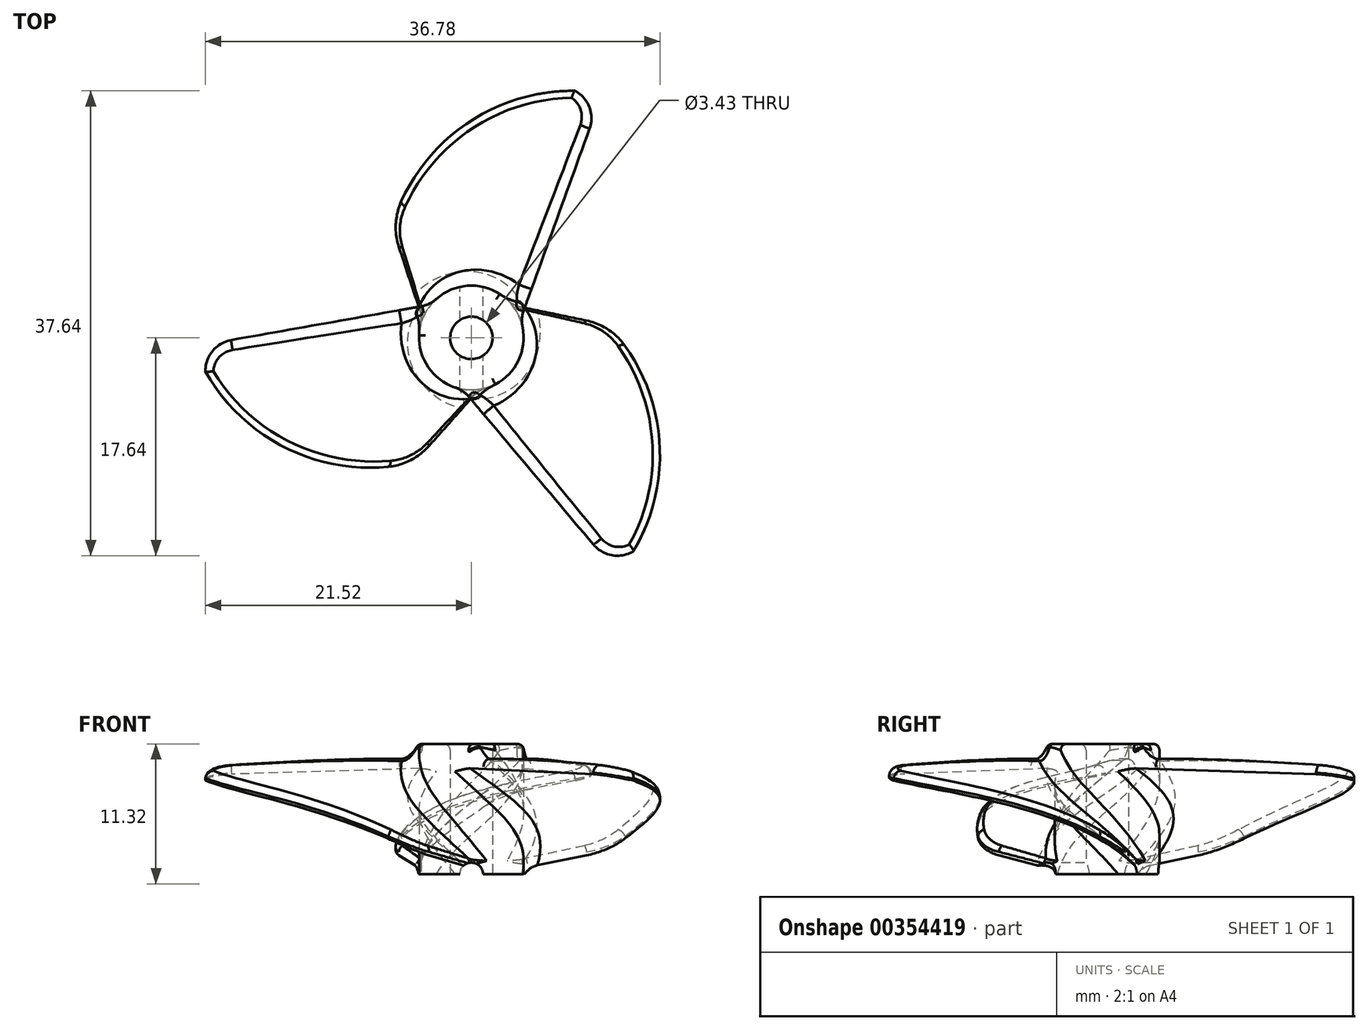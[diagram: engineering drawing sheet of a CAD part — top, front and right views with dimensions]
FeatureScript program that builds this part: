
annotation { "Feature Type Name" : "Feature", "Feature Type Description" : "" }
export const myFeature = defineFeature(function(context is Context, id is Id, definition is map)
    precondition{}
    {
        {
            var Q0;
            Q0=qCreatedBy(makeId("Top.planeOp"),FACE);
            var sketch = newSketch(context, id + "F0", { "sketchPlane" : qUnion([Q0])});
            skCircle(sketch, "E0", {"center": v(0, 0) * mm, "radius": 4.23 * mm});
            skSolve(sketch);
        }
        {
            var Q0;
            Q0 = qSketchRegion(id + "F0", true);
            extrude(context, id + "F1", {"entities" : qUnion([Q0]), "depth" : 10.54 * mm});
        }
        {
            var Q0;
            Q0=qCreatedBy(makeId("Front.planeOp"),FACE);
            var sketch = newSketch(context, id + "F2", { "sketchPlane" : qUnion([Q0])});
            skLineSegment(sketch, "E1", {"start": v(3.43, 10.54) * mm, "end": v(-3.43, 0.5) * mm});
            skLineSegment(sketch, "E2", {"start": v(-3.43, 0) * mm, "end": v(3.43, 8.64) * mm});
            skLineSegment(sketch, "E3", {"start": v(3.43, 8.64) * mm, "end": v(3.43, 10.54) * mm});
            skLineSegment(sketch, "E4", {"start": v(3.43, 10.54) * mm, "end": v(0, 10.54) * mm, "construction": true});
            skLineSegment(sketch, "E5", {"start": v(0, 10.54) * mm, "end": v(-3.43, 10.54) * mm, "construction": true});
            skLineSegment(sketch, "E6", {"start": v(-3.43, 10.54) * mm, "end": v(-3.43, 0.5) * mm, "construction": true});
            skLineSegment(sketch, "E7", {"start": v(-3.43, 0) * mm, "end": v(-3.43, 0.5) * mm});
            skSolve(sketch);
        }
        {
            var Q0;
            Q0=qCreatedBy(makeId("Front.planeOp"),FACE);
            cPlane(context, id + "F3", {"entities" : qUnion([Q0]), "cplaneType" : CPlaneType.OFFSET, "offset" : 20.32 * mm, "oppositeDirection" : true, "width" : 152.4 * mm, "height" : 152.4 * mm});
        }
        {
            var Q0;
            Q0=qCreatedBy(id+"F3.planeOp",FACE);
            var sketch = newSketch(context, id + "F4", { "sketchPlane" : qUnion([Q0])});
            skLineSegment(sketch, "E8", {"start": v(10.8, 8.76) * mm, "end": v(-10.16, 5) * mm});
            skLineSegment(sketch, "E9", {"start": v(-10.16, 5) * mm, "end": v(-10.16, 4.22) * mm});
            skLineSegment(sketch, "E10", {"start": v(-10.16, 4.22) * mm, "end": v(10.8, 7.99) * mm});
            skLineSegment(sketch, "E11", {"start": v(10.8, 7.99) * mm, "end": v(10.8, 8.76) * mm});
            skSolve(sketch);
        }
        {
            var Q0;
            Q0=makeQuery(id+"F2.imprint","IMPRINT",FACE,{"disambiguationData":[TD([[makeQuery(id+"F2.imprint","IMPRINT",EDGE,{"derivedFrom":sQuery(id+"F2.wireOp",EDGE,"E1")}),1.0]])]});
            var Q1;
            Q1=makeQuery(id+"F4.imprint","IMPRINT",FACE,{"disambiguationData":[TD([[makeQuery(id+"F4.imprint","IMPRINT",EDGE,{"derivedFrom":sQuery(id+"F4.wireOp",EDGE,"E8")}),1.0]])]});
            loft(context, id + "F5", {"sheetProfilesArray" : [{ "sheetProfileEntities" : qUnion([Q0]) }, { "sheetProfileEntities" : qUnion([Q1]) }]});
        }
        {
            var Q0;
            Q0=makeQuery(id+"F5.opLoft","MID_CAP_EDGE",EDGE,{"disambiguationData":[OSD([sQuery(id+"F4.wireOp",EDGE,"E8"),sQuery(id+"F4.wireOp",EDGE,"E10"),sQuery(id+"F4.wireOp",EDGE,"E11")])],"capPos":1.0});
            fillet(context, id + "F6", {"entities" : qUnion([Q0]), "radius" : 2.54 * mm, "tangentPropagation" : true, "allowEdgeOverflow" : false});
        }
        {
            var Q0;
            Q0=qCreatedBy(makeId("Top.planeOp"),FACE);
            var sketch = newSketch(context, id + "F7", { "sketchPlane" : qUnion([Q0])});
            skArc(sketch, "E12", {"start": v(10.23, 19.86) * mm, "mid": v(-0.6, 17.2) * mm, "end": v(-6.71, 7.88) * mm});
            skLineSegment(sketch, "E13", {"start": v(-6.71, 7.88) * mm, "end": v(-17.65, 28.01) * mm});
            skLineSegment(sketch, "E14", {"start": v(-17.65, 28.01) * mm, "end": v(12.3, 32.12) * mm});
            skLineSegment(sketch, "E15", {"start": v(12.3, 32.12) * mm, "end": v(10.23, 19.86) * mm});
            skSolve(sketch);
        }
        {
            var Q0;
            Q0 = qSketchRegion(id + "F7", true);
            extrude(context, id + "F8", {"entities" : qUnion([Q0]), "operationType" : NewBodyOperationType.REMOVE, "depth" : 50.8 * mm});
        }
        {
            var Q0;
            Q0=makeQuery(id+"F8.boolean.opBoolean","INTERSECT",EDGE,{"derivedFrom":[makeQuery(id+"F5.opLoft","SWEPT_FACE",FACE,{"disambiguationData":[OSD([sQuery(id+"F2.wireOp",EDGE,"E1"),sQuery(id+"F2.wireOp",EDGE,"vgnnuIFg-lXOL-v0tE-bj0G-pIZIy2lSMrQo"),sQuery(id+"F2.wireOp",EDGE,"E2"),sQuery(id+"F4.wireOp",EDGE,"E8"),sQuery(id+"F4.wireOp",EDGE,"E9"),sQuery(id+"F4.wireOp",EDGE,"E10")])]}),makeQuery(id+"F8.opExtrude","SWEPT_FACE",FACE,{"disambiguationData":[OSD([sQuery(id+"F7.wireOp",EDGE,"E12")])]})]});
            fillet(context, id + "F9", {"entities" : qUnion([Q0]), "radius" : 5.08 * mm, "tangentPropagation" : true, "allowEdgeOverflow" : false});
        }
        {
            var Q0;
            Q0=makeQuery(id+"F1.opExtrude","SWEPT_BODY",BODY,{"disambiguationData":[OSD([sQuery(id+"F0.wireOp",EDGE,"E0")])]});
            var Q1;
            Q1=makeQuery(id+"F5.opLoft","SWEPT_BODY",BODY,{"disambiguationData":[OSD([makeQuery(id+"F2.imprint","IMPRINT",FACE,{"disambiguationData":[TD([[makeQuery(id+"F2.imprint","IMPRINT",EDGE,{"derivedFrom":sQuery(id+"F2.wireOp",EDGE,"E1")}),1.0]])]}),makeQuery(id+"F4.imprint","IMPRINT",FACE,{"disambiguationData":[TD([[makeQuery(id+"F4.imprint","IMPRINT",EDGE,{"derivedFrom":sQuery(id+"F4.wireOp",EDGE,"E8")}),1.0]])]})])]});
            booleanBodies(context, id + "F10", {"operationType" : BooleanOperationType.UNION, "tools" : qUnion([Q0, Q1])});
        }
        {
            var Q0;
            Q0=makeQuery(id+"F10.opBoolean","INTERSECT",EDGE,{"derivedFrom":[makeQuery(id+"F1.opExtrude","SWEPT_FACE",FACE,{"disambiguationData":[OSD([sQuery(id+"F0.wireOp",EDGE,"E0")])]}),makeQuery(id+"F5.opLoft","SWEPT_FACE",FACE,{"disambiguationData":[OSD([sQuery(id+"F2.wireOp",EDGE,"vgnnuIFg-lXOL-v0tE-bj0G-pIZIy2lSMrQo"),sQuery(id+"F2.wireOp",EDGE,"E2"),sQuery(id+"F2.wireOp",EDGE,"E3"),sQuery(id+"F4.wireOp",EDGE,"E9"),sQuery(id+"F4.wireOp",EDGE,"E10"),sQuery(id+"F4.wireOp",EDGE,"E11")])]})]});
            var Q1;
            Q1=makeQuery(id+"F10.opBoolean","INTERSECT",EDGE,{"derivedFrom":[makeQuery(id+"F1.opExtrude","SWEPT_FACE",FACE,{"disambiguationData":[OSD([sQuery(id+"F0.wireOp",EDGE,"E0")])]}),makeQuery(id+"F5.opLoft","SWEPT_FACE",FACE,{"disambiguationData":[OSD([sQuery(id+"F2.wireOp",EDGE,"E1"),sQuery(id+"F2.wireOp",EDGE,"vgnnuIFg-lXOL-v0tE-bj0G-pIZIy2lSMrQo"),sQuery(id+"F2.wireOp",EDGE,"E3"),sQuery(id+"F4.wireOp",EDGE,"E8"),sQuery(id+"F4.wireOp",EDGE,"E9"),sQuery(id+"F4.wireOp",EDGE,"E11")])]})]});
            fillet(context, id + "F11", {"entities" : qUnion([Q0, Q1]), "radius" : 1.27 * mm, "tangentPropagation" : true, "allowEdgeOverflow" : false});
        }
        {
            var Q0;
            Q0=makeQuery(id+"F10.opBoolean","INTERSECT",EDGE,{"derivedFrom":[makeQuery(id+"F1.opExtrude","SWEPT_FACE",FACE,{"disambiguationData":[OSD([sQuery(id+"F0.wireOp",EDGE,"E0")])]}),makeQuery(id+"F5.opLoft","SWEPT_FACE",FACE,{"disambiguationData":[OSD([sQuery(id+"F2.wireOp",EDGE,"E1"),sQuery(id+"F2.wireOp",EDGE,"E2"),sQuery(id+"F2.wireOp",EDGE,"E3"),sQuery(id+"F4.wireOp",EDGE,"E8"),sQuery(id+"F4.wireOp",EDGE,"E10"),sQuery(id+"F4.wireOp",EDGE,"E11")])]})]});
            fillet(context, id + "F12", {"entities" : qUnion([Q0]), "radius" : 2.54 * mm, "tangentPropagation" : true, "allowEdgeOverflow" : false});
        }
        {
            var Q0;
            Q0=makeQuery(id+"F10.opBoolean","INTERSECT",EDGE,{"derivedFrom":[makeQuery(id+"F1.opExtrude","SWEPT_FACE",FACE,{"disambiguationData":[OSD([sQuery(id+"F0.wireOp",EDGE,"E0")])]}),makeQuery(id+"F5.opLoft","SWEPT_FACE",FACE,{"disambiguationData":[OSD([sQuery(id+"F2.wireOp",EDGE,"E1"),sQuery(id+"F2.wireOp",EDGE,"vgnnuIFg-lXOL-v0tE-bj0G-pIZIy2lSMrQo"),sQuery(id+"F2.wireOp",EDGE,"E2"),sQuery(id+"F4.wireOp",EDGE,"E8"),sQuery(id+"F4.wireOp",EDGE,"E9"),sQuery(id+"F4.wireOp",EDGE,"E10")])]})]});
            fillet(context, id + "F13", {"entities" : qUnion([Q0]), "radius" : 2.54 * mm, "tangentPropagation" : true, "allowEdgeOverflow" : false});
        }
        {
            var Q0;
            Q0=makeQuery(id+"F5.opLoft","SWEPT_EDGE",EDGE,{"disambiguationData":[OSD([sQuery(id+"F2.wireOp",EDGE,"E1"),sQuery(id+"F2.wireOp",EDGE,"E3"),sQuery(id+"F4.wireOp",EDGE,"E8"),sQuery(id+"F4.wireOp",EDGE,"E11")])]});
            var Q1;
            {var subQ0=sQuery(id+"F4.wireOp",EDGE,"E11");var subQ1=sQuery(id+"F4.wireOp",EDGE,"E8");var subQ2=sQuery(id+"F2.wireOp",EDGE,"E3");var subQ3=sQuery(id+"F2.wireOp",EDGE,"E1");Q1=makeQuery(id+"F11.opFillet","BLEND_EDGE",EDGE,{"blendedFrom":[makeQuery(id+"F10.opBoolean","INTERSECT",EDGE,{"derivedFrom":[makeQuery(id+"F1.opExtrude","SWEPT_FACE",FACE,{"disambiguationData":[OSD([sQuery(id+"F0.wireOp",EDGE,"E0")])]}),makeQuery(id+"F5.opLoft","SWEPT_FACE",FACE,{"disambiguationData":[OSD([subQ3,sQuery(id+"F2.wireOp",EDGE,"vgnnuIFg-lXOL-v0tE-bj0G-pIZIy2lSMrQo"),subQ2,subQ1,sQuery(id+"F4.wireOp",EDGE,"E9"),subQ0])]})]}),makeQuery(id+"F5.opLoft","SWEPT_FACE",FACE,{"disambiguationData":[OSD([subQ3,sQuery(id+"F2.wireOp",EDGE,"E2"),subQ2,subQ1,sQuery(id+"F4.wireOp",EDGE,"E10"),subQ0])]})],"blendedInto":[makeQuery(id+"F5.opLoft","SWEPT_FACE",FACE,{"disambiguationData":[OSD([subQ3,sQuery(id+"F2.wireOp",EDGE,"E2"),subQ2,subQ1,sQuery(id+"F4.wireOp",EDGE,"E10"),subQ0])]})]});}
            var Q2;
            {var subQ0=sQuery(id+"F4.wireOp",EDGE,"E11");var subQ1=sQuery(id+"F4.wireOp",EDGE,"E8");Q2=makeQuery(id+"F6.opFillet","BLEND_EDGE",EDGE,{"blendedFrom":[makeQuery(id+"F5.opLoft","MID_CAP_EDGE",EDGE,{"disambiguationData":[OSD([subQ1,sQuery(id+"F4.wireOp",EDGE,"E10"),subQ0])],"capPos":1.0}),makeQuery(id+"F5.opLoft","SWEPT_FACE",FACE,{"disambiguationData":[OSD([sQuery(id+"F2.wireOp",EDGE,"E1"),sQuery(id+"F2.wireOp",EDGE,"vgnnuIFg-lXOL-v0tE-bj0G-pIZIy2lSMrQo"),sQuery(id+"F2.wireOp",EDGE,"E3"),subQ1,sQuery(id+"F4.wireOp",EDGE,"E9"),subQ0])]})],"blendedInto":[makeQuery(id+"F5.opLoft","SWEPT_FACE",FACE,{"disambiguationData":[OSD([sQuery(id+"F2.wireOp",EDGE,"E1"),sQuery(id+"F2.wireOp",EDGE,"vgnnuIFg-lXOL-v0tE-bj0G-pIZIy2lSMrQo"),sQuery(id+"F2.wireOp",EDGE,"E3"),subQ1,sQuery(id+"F4.wireOp",EDGE,"E9"),subQ0])]})]});}
            var Q3;
            Q3=makeQuery(id+"F8.boolean.opBoolean","INTERSECT",EDGE,{"derivedFrom":[makeQuery(id+"F5.opLoft","SWEPT_FACE",FACE,{"disambiguationData":[OSD([sQuery(id+"F2.wireOp",EDGE,"E1"),sQuery(id+"F2.wireOp",EDGE,"vgnnuIFg-lXOL-v0tE-bj0G-pIZIy2lSMrQo"),sQuery(id+"F2.wireOp",EDGE,"E3"),sQuery(id+"F4.wireOp",EDGE,"E8"),sQuery(id+"F4.wireOp",EDGE,"E9"),sQuery(id+"F4.wireOp",EDGE,"E11")])]}),makeQuery(id+"F8.opExtrude","SWEPT_FACE",FACE,{"disambiguationData":[OSD([sQuery(id+"F7.wireOp",EDGE,"E12")])]})]});
            var Q4;
            Q4=makeQuery(id+"F5.opLoft","SWEPT_EDGE",EDGE,{"disambiguationData":[OSD([sQuery(id+"F2.wireOp",EDGE,"E1"),sQuery(id+"F2.wireOp",EDGE,"vgnnuIFg-lXOL-v0tE-bj0G-pIZIy2lSMrQo"),sQuery(id+"F4.wireOp",EDGE,"E8"),sQuery(id+"F4.wireOp",EDGE,"E9")])]});
            fillet(context, id + "F14", {"entities" : qUnion([Q0, Q1, Q2, Q3, Q4]), "radius" : 0.64 * mm, "tangentPropagation" : true, "allowEdgeOverflow" : false});
        }
        {
            var Q0;
            Q0=makeQuery(id+"F1.opExtrude","SWEPT_BODY",BODY,{"disambiguationData":[OSD([sQuery(id+"F0.wireOp",EDGE,"E0")])]});
            var Q1;
            Q1=makeQuery(id+"F1.opExtrude","CAP_EDGE",EDGE,{"disambiguationData":[OSD([sQuery(id+"F0.wireOp",EDGE,"E0")])],"isStart":false});
            circularPattern(context, id + "F15", {"entities" : qUnion([Q0]), "axis" : qUnion([Q1]), "angle" : 360 * degree, "instanceCount" : 3, "equalSpace" : true});
        }
        {
            var Q0;
            Q0=makeQuery(id+"F1.opExtrude","SWEPT_BODY",BODY,{"disambiguationData":[OSD([sQuery(id+"F0.wireOp",EDGE,"E0")])]});
            var Q1;
            Q1=makeQuery(id+"F15.opPattern","COPY",BODY,{"derivedFrom":makeQuery(id+"F1.opExtrude","SWEPT_BODY",BODY,{"disambiguationData":[OSD([sQuery(id+"F0.wireOp",EDGE,"E0")])]}),"instanceName":"2"});
            var Q2;
            Q2=makeQuery(id+"F15.opPattern","COPY",BODY,{"derivedFrom":makeQuery(id+"F1.opExtrude","SWEPT_BODY",BODY,{"disambiguationData":[OSD([sQuery(id+"F0.wireOp",EDGE,"E0")])]}),"instanceName":"1"});
            booleanBodies(context, id + "F16", {"operationType" : BooleanOperationType.UNION, "tools" : qUnion([Q0, Q1, Q2])});
        }
        {
            var Q0;
            {var subQ0=makeQuery(id+"F1.opExtrude","CAP_FACE",FACE,{"disambiguationData":[OSD([sQuery(id+"F0.wireOp",EDGE,"E0")])],"isStart":true});Q0=makeQuery(id+"F16.opBoolean","MERGE",FACE,{"derivedFrom":[subQ0,makeQuery(id+"F15.opPattern","COPY",FACE,{"derivedFrom":subQ0,"instanceName":"1"}),makeQuery(id+"F15.opPattern","COPY",FACE,{"derivedFrom":subQ0,"instanceName":"2"})]});}
            var sketch = newSketch(context, id + "F17", { "sketchPlane" : qUnion([Q0])});
            skCircle(sketch, "E16", {"center": v(0, 0) * mm, "radius": 1.71 * mm});
            skSolve(sketch);
        }
        {
            var Q0;
            Q0 = qSketchRegion(id + "F17", true);
            extrude(context, id + "F18", {"entities" : qUnion([Q0]), "operationType" : NewBodyOperationType.REMOVE, "oppositeDirection" : true, "depth" : 25.4 * mm});
        }
        {
            var Q0;
            Q0=qCreatedBy(id+"F3.planeOp",FACE);
            var sketch = newSketch(context, id + "F19", { "sketchPlane" : qUnion([Q0])});
            skCircle(sketch, "E17", {"center": v(0, 0) * mm, "radius": 0.94 * mm});
            skSolve(sketch);
        }
        {
            var Q0;
            Q0 = qSketchRegion(id + "F19", true);
            extrude(context, id + "F20", {"entities" : qUnion([Q0]), "operationType" : NewBodyOperationType.REMOVE, "depth" : 59.69 * mm});
        }
        {
            var Q0;
            {var subQ0=makeQuery(id+"F1.opExtrude","CAP_FACE",FACE,{"disambiguationData":[OSD([sQuery(id+"F0.wireOp",EDGE,"E0")])],"isStart":false});Q0=makeQuery(id+"F16.opBoolean","MERGE",FACE,{"derivedFrom":[subQ0,makeQuery(id+"F15.opPattern","COPY",FACE,{"derivedFrom":subQ0,"instanceName":"1"}),makeQuery(id+"F15.opPattern","COPY",FACE,{"derivedFrom":subQ0,"instanceName":"2"})]});}
            fillet(context, id + "F21", {"entities" : qUnion([Q0]), "radius" : 0.5 * mm, "tangentPropagation" : true, "allowEdgeOverflow" : false});
        }
    });
